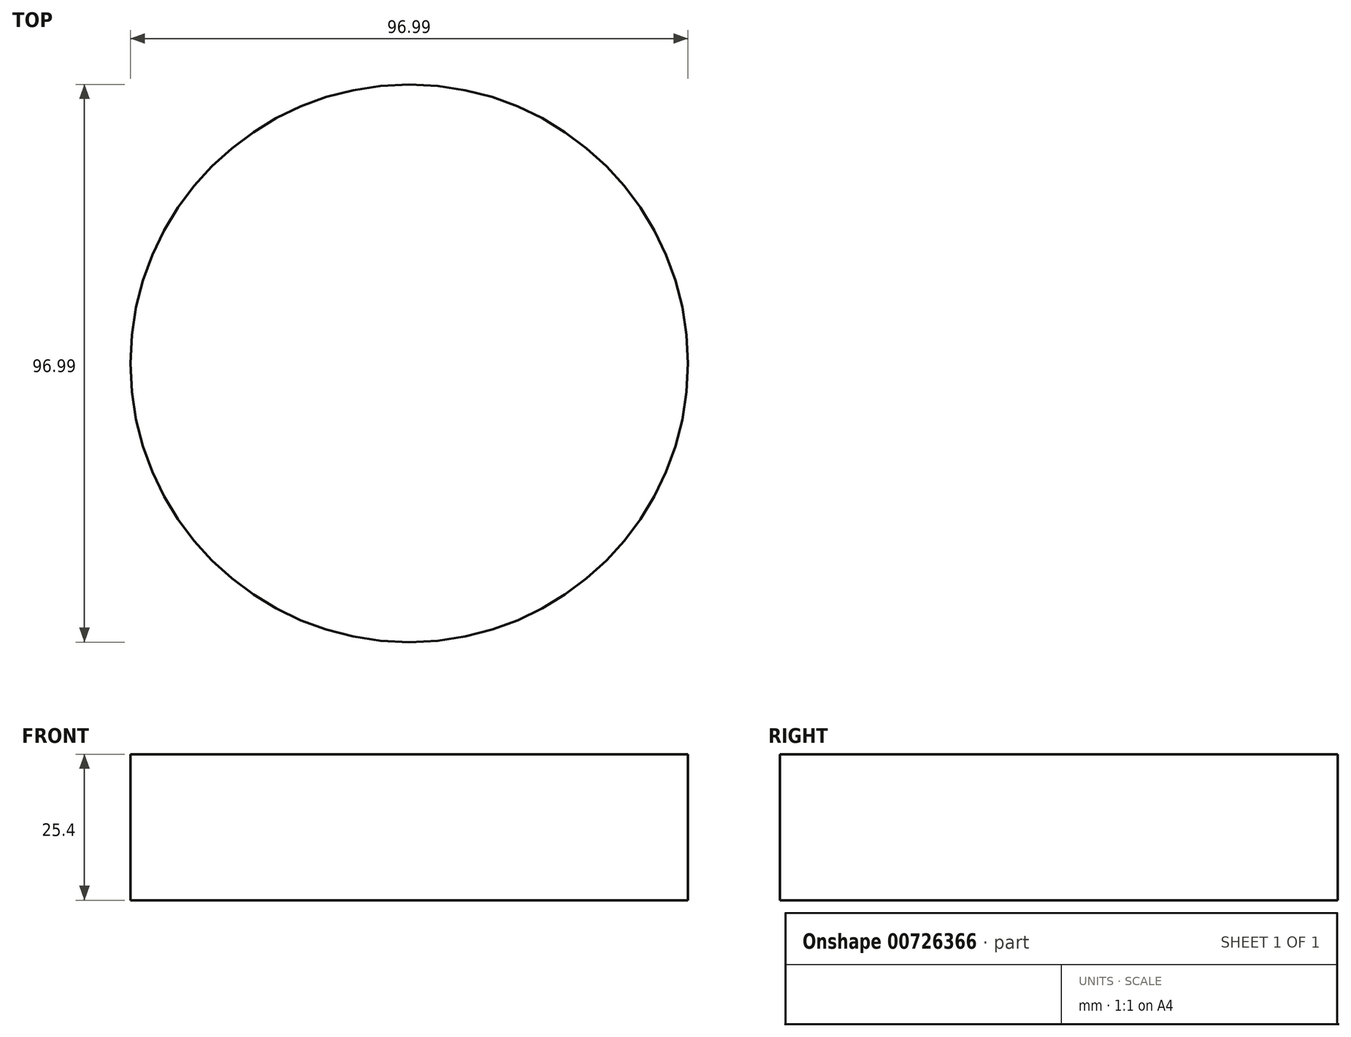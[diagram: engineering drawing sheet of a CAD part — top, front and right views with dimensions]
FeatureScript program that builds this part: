
annotation { "Feature Type Name" : "Feature", "Feature Type Description" : "" }
export const myFeature = defineFeature(function(context is Context, id is Id, definition is map)
    precondition{}
    {
        {
            var Q0;
            Q0=qCreatedBy(makeId("Top.planeOp"),FACE);
            var sketch = newSketch(context, id + "F0", { "sketchPlane" : qUnion([Q0])});
            skCircle(sketch, "E0", {"center": v(30.72, -22.23) * mm, "radius": 48.5 * mm});
            skSolve(sketch);
        }
        {
            var Q0;
            Q0=makeQuery(id+"F0.imprint","IMPRINT",FACE,{"disambiguationData":[TD([[makeQuery(id+"F0.imprint","IMPRINT",EDGE,{"derivedFrom":sQuery(id+"F0.wireOp",EDGE,"E0")}),1.0]])]});
            extrude(context, id + "F1", {"entities" : qUnion([Q0]), "depth" : 25.4 * mm, "offsetDistance" : 25.4 * mm});
        }
    });
